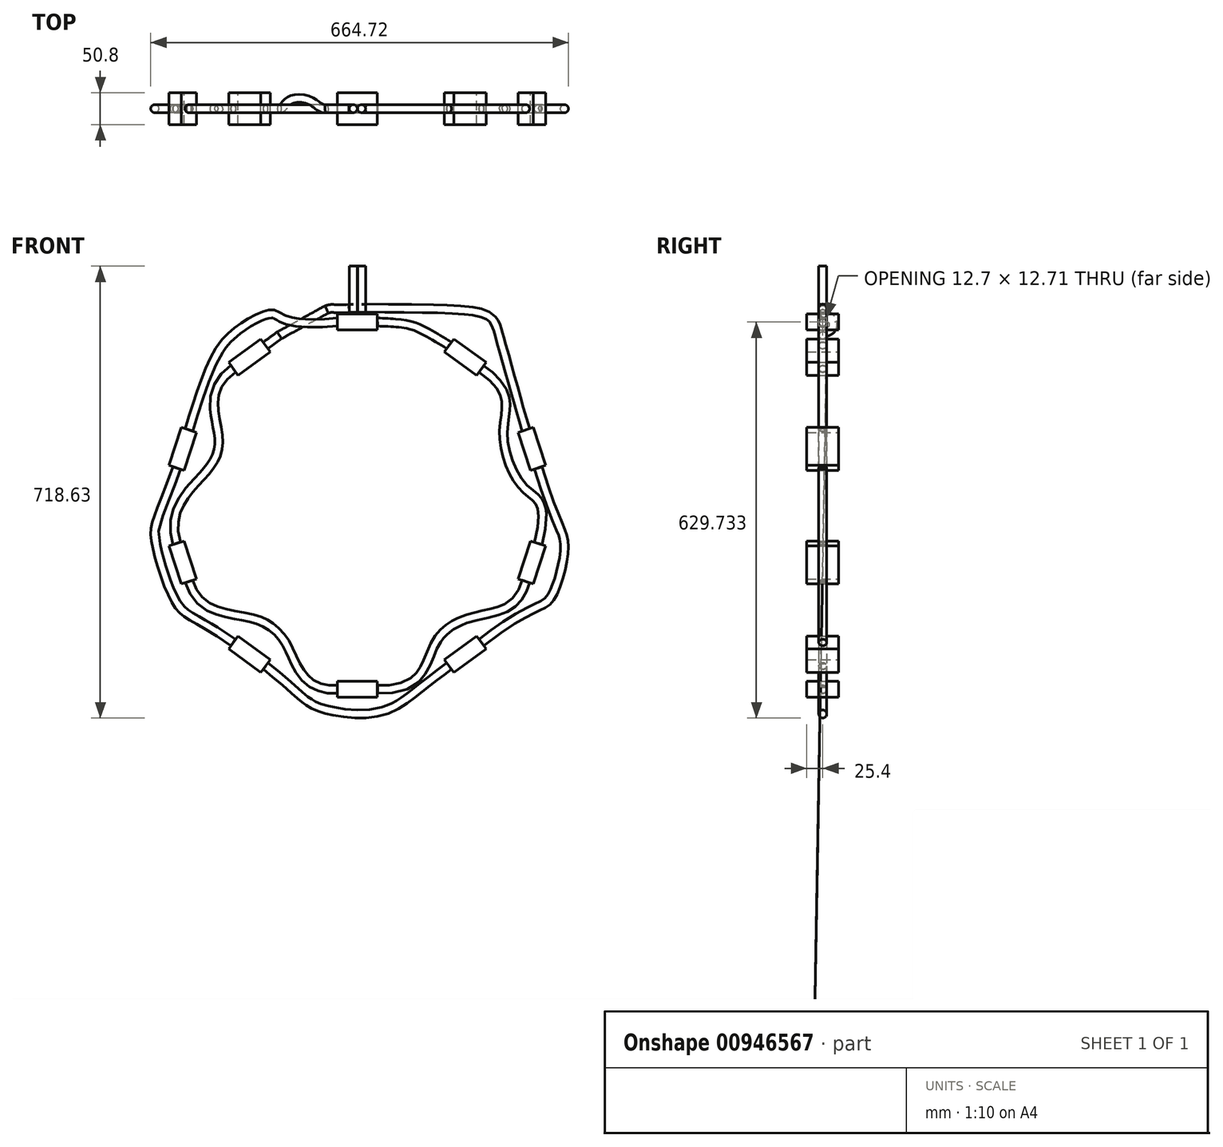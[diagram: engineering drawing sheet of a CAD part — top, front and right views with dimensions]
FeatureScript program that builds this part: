
annotation { "Feature Type Name" : "Feature", "Feature Type Description" : "" }
export const myFeature = defineFeature(function(context is Context, id is Id, definition is map)
    precondition{}
    {
        {
            var Q0;
            Q0=qCreatedBy(makeId("Front.planeOp"),FACE);
            var sketch = newSketch(context, id + "F0", { "sketchPlane" : qUnion([Q0])});
            skCircle(sketch, "E0", {"center": v(0, 0) * mm, "radius": 279.4 * mm});
            skCircle(sketch, "E1", {"center": v(0, 0) * mm, "radius": 304.8 * mm});
            skLineSegment(sketch, "E2", {"start": v(0, 279.4) * mm, "end": v(0, 304.8) * mm, "construction": true});
            skLineSegment(sketch, "E3.bottom", {"start": v(31.75, 304.8) * mm, "end": v(-31.75, 304.8) * mm});
            skLineSegment(sketch, "E3.top", {"start": v(31.75, 279.4) * mm, "end": v(-31.75, 279.4) * mm});
            skLineSegment(sketch, "E3.left", {"start": v(31.75, 304.8) * mm, "end": v(31.75, 279.4) * mm});
            skLineSegment(sketch, "E3.right", {"start": v(-31.75, 304.8) * mm, "end": v(-31.75, 279.4) * mm});
            skPoint(sketch, "E3.middle", {"position": v(0, 292.1) * mm});
            skSolve(sketch);
        }
        {
            var Q0;
            {var subQ0=sQuery(id+"F0.wireOp",EDGE,"E3.bottom");var subQ1=sQuery(id+"F0.wireOp",EDGE,"E1");var subQ2=makeQuery(id+"F0.imprint","INTERSECT",VERTEX,{"derivedFrom":[subQ1,subQ0]});Q0=makeQuery(id+"F0.imprint","IMPRINT",FACE,{"disambiguationData":[TD([[makeQuery(id+"F0.imprint","IMPRINT",EDGE,{"disambiguationData":[TD([[subQ2,1.0]])],"derivedFrom":subQ1}),-1.0]])]});}
            var Q1;
            {var subQ0=sQuery(id+"F0.wireOp",EDGE,"E3.bottom");var subQ1=sQuery(id+"F0.wireOp",EDGE,"E1");var subQ2=makeQuery(id+"F0.imprint","INTERSECT",VERTEX,{"derivedFrom":[subQ1,subQ0]});Q1=makeQuery(id+"F0.imprint","IMPRINT",FACE,{"disambiguationData":[TD([[makeQuery(id+"F0.imprint","IMPRINT",EDGE,{"disambiguationData":[TD([[subQ2,-1.0]])],"derivedFrom":subQ1}),-1.0]])]});}
            var Q2;
            {var subQ4=sQuery(id+"F0.wireOp",EDGE,"E1");var subQ5=makeQuery(id+"F0.imprint","INTERSECT",VERTEX,{"derivedFrom":[subQ4,sQuery(id+"F0.wireOp",EDGE,"E3.bottom")]});Q2=makeQuery(id+"F0.imprint","IMPRINT",FACE,{"disambiguationData":[TD([[makeQuery(id+"F0.imprint","IMPRINT",EDGE,{"disambiguationData":[TD([[subQ5,1.0]])],"derivedFrom":subQ4}),1.0]])]});}
            extrude(context, id + "F1", {"entities" : qUnion([Q0, Q1, Q2]), "endBound" : BoundingType.SYMMETRIC, "depth" : 50.8 * mm, "offsetDistance" : 25.4 * mm});
        }
        {
            var Q0;
            Q0=makeQuery(id+"F1.opExtrude","SWEPT_FACE",FACE,{"disambiguationData":[OSD([sQuery(id+"F0.wireOp",EDGE,"E3.left")])]});
            var sketch = newSketch(context, id + "F2", { "sketchPlane" : qUnion([Q0])});
            skCircle(sketch, "E4", {"center": v(0, 292.1) * mm, "radius": 4.76 * mm});
            skPoint(sketch, "E4.centerSnap0", {"position": v(-25.4, 292.1) * mm});
            skPoint(sketch, "E4.centerSnap1", {"position": v(0, 304.8) * mm});
            skCircle(sketch, "E5", {"center": v(0, 292.1) * mm, "radius": 6.35 * mm});
            skSolve(sketch);
        }
        {
            var Q0;
            Q0=qSketchRegion(id+"F2",true);
            var Q1;
            Q1=makeQuery(id+"F2.imprint","IMPRINT",FACE,{"disambiguationData":[TD([[makeQuery(id+"F2.imprint","IMPRINT",EDGE,{"derivedFrom":sQuery(id+"F2.wireOp",EDGE,"E4")}),1.0]])]});
            extrude(context, id + "F3", {"entities" : qUnion([Q0, Q1]), "operationType" : NewBodyOperationType.ADD, "depth" : 0.25 * mm, "offsetDistance" : 25.4 * mm});
        }
        {
            var Q0;
            Q0=makeQuery(id+"F1.opExtrude","SWEPT_FACE",FACE,{"disambiguationData":[OSD([sQuery(id+"F0.wireOp",EDGE,"E3.right")])]});
            var sketch = newSketch(context, id + "F4", { "sketchPlane" : qUnion([Q0])});
            skCircle(sketch, "E6", {"center": v(0, 292.1) * mm, "radius": 6.35 * mm});
            skSolve(sketch);
        }
        {
            var Q0;
            Q0=qSketchRegion(id+"F4",true);
            extrude(context, id + "F5", {"entities" : qUnion([Q0]), "operationType" : NewBodyOperationType.ADD, "depth" : 0.25 * mm, "offsetDistance" : 25.4 * mm});
        }
        {
            var Q0;
            Q0=makeQuery(id+"F1.opExtrude","SWEPT_BODY",BODY,{"disambiguationData":[OSD([sQuery(id+"F0.wireOp",EDGE,"E3.bottom"),sQuery(id+"F0.wireOp",EDGE,"E3.top"),sQuery(id+"F0.wireOp",EDGE,"E3.left"),sQuery(id+"F0.wireOp",EDGE,"E3.right")])]});
            var Q1;
            Q1=sQuery(id+"F0.wireOp",EDGE,"E0");
            circularPattern(context, id + "F6", {"operationType" : NewBodyOperationType.ADD, "entities" : qUnion([Q0]), "axis" : qUnion([Q1]), "angle" : 360 * degree, "instanceCount" : 10, "equalSpace" : true});
        }
        {
            var Q0;
            Q0=makeQuery(id+"F1.opExtrude","SWEPT_FACE",FACE,{"disambiguationData":[OSD([sQuery(id+"F0.wireOp",EDGE,"E3.bottom")])]});
            cPlane(context, id + "F7", {"entities" : qUnion([Q0]), "cplaneType" : CPlaneType.OFFSET, "offset" : 76.2 * mm, "width" : 152.4 * mm, "height" : 152.4 * mm});
        }
        {
            var Q0;
            Q0=qCreatedBy(id+"F7.planeOp",FACE);
            var sketch = newSketch(context, id + "F8", { "sketchPlane" : qUnion([Q0])});
            skCircle(sketch, "E7", {"center": v(6.6, 0) * mm, "radius": 6.35 * mm});
            skSolve(sketch);
        }
        {
            var Q0;
            Q0=makeQuery(id+"F8.imprint","IMPRINT",FACE,{"disambiguationData":[TD([[makeQuery(id+"F8.imprint","IMPRINT",EDGE,{"derivedFrom":sQuery(id+"F8.wireOp",EDGE,"tEIZt6W4-ahLr-2Sv8-WXze-j2Jn50dJCbSE")}),1.0]])]});
            var Q1;
            Q1=makeQuery(id+"F8.imprint","IMPRINT",FACE,{"disambiguationData":[TD([[makeQuery(id+"F8.imprint","IMPRINT",EDGE,{"derivedFrom":sQuery(id+"F8.wireOp",EDGE,"E7")}),1.0]])]});
            extrude(context, id + "F9", {"entities" : qUnion([Q0, Q1]), "oppositeDirection" : true, "depth" : 73.66 * mm, "offsetDistance" : 25.4 * mm});
        }
        {
            var Q0;
            Q0=makeQuery(id+"F9.opExtrude","CAP_FACE",FACE,{"disambiguationData":[OSD([sQuery(id+"F8.wireOp",EDGE,"E7")])],"isStart":false});
            var sketch = newSketch(context, id + "F10", { "sketchPlane" : qUnion([Q0])});
            skLineSegment(sketch, "E8", {"start": v(6.6, 0) * mm, "end": v(6.6, -6.35) * mm});
            skLineSegment(sketch, "E9", {"start": v(6.6, -6.35) * mm, "end": v(12.95, -6.35) * mm});
            skLineSegment(sketch, "E10", {"start": v(12.95, -6.35) * mm, "end": v(12.95, 6.35) * mm});
            skLineSegment(sketch, "E11", {"start": v(12.95, 6.35) * mm, "end": v(6.6, 6.35) * mm});
            skLineSegment(sketch, "E12", {"start": v(6.6, 6.35) * mm, "end": v(6.6, 0) * mm});
            skSolve(sketch);
        }
        {
            var Q0;
            Q0=qSketchRegion(id+"F10",true);
            extrude(context, id + "F11", {"entities" : qUnion([Q0]), "operationType" : NewBodyOperationType.ADD, "oppositeDirection" : true, "depth" : 12.7 * mm, "offsetDistance" : 25.4 * mm});
        }
        {
            var Q0;
            Q0=makeQuery(id+"F11.opExtrude","SWEPT_FACE",FACE,{"disambiguationData":[OSD([sQuery(id+"F10.wireOp",EDGE,"E10")])]});
            var sketch = newSketch(context, id + "F12", { "sketchPlane" : qUnion([Q0])});
            skCircle(sketch, "E13", {"center": v(0, 313.7) * mm, "radius": 4.76 * mm});
            skPoint(sketch, "E13.centerSnap0", {"position": v(6.35, 313.7) * mm});
            skSolve(sketch);
        }
        {
            var Q0;
            Q0=makeQuery(id+"F11.opExtrude","SWEPT_FACE",FACE,{"disambiguationData":[OSD([sQuery(id+"F10.wireOp",EDGE,"E10")])]});
            var sketch = newSketch(context, id + "F13", { "sketchPlane" : qUnion([Q0])});
            skCircle(sketch, "E14", {"center": v(0, 313.7) * mm, "radius": 6.35 * mm});
            skSolve(sketch);
        }
        {
            var Q0;
            Q0 = qSketchRegion(id + "F13", true);
            extrude(context, id + "F14", {"entities" : qUnion([Q0]), "operationType" : NewBodyOperationType.ADD, "depth" : 0.25 * mm, "offsetDistance" : 25.4 * mm});
        }
        {
            var Q0;
            Q0=makeQuery(id+"F9.opExtrude","SWEPT_BODY",BODY,{"disambiguationData":[OSD([sQuery(id+"F8.wireOp",EDGE,"E7")])]});
            var Q1;
            Q1=qCreatedBy(makeId("Right.planeOp"),FACE);
            mirror(context, id + "F15", {"entities" : qUnion([Q0]), "mirrorPlane" : qUnion([Q1])});
        }
        {
            var Q0;
            Q0=makeQuery(id+"F0.imprint","IMPRINT",FACE,{"disambiguationData":[TD([[makeQuery(id+"F0.imprint","IMPRINT",EDGE,{"derivedFrom":sQuery(id+"F0.wireOp",EDGE,"E0")}),1.0]])]});
            var sketch = newSketch(context, id + "F16", { "sketchPlane" : qUnion([Q0])});
            skFitSpline(sketch, "E15", {"points": [v(12.47, 313.93) * mm, v(226.12, 268.52) * mm, v(267.78, 120.27) * mm], "startDerivative": vector(1120.98, -8.53) * mm, "endDerivative": vector(74.4, -254) * mm});
            skFitSpline(sketch, "E16", {"points": [v(287.61, 60.07) * mm, v(329.49, -68.55) * mm, v(308.97, -144.06) * mm, v(197.38, -217.65) * mm], "startDerivative": vector(250.83, -825.95) * mm, "endDerivative": vector(-693.05, -541.05) * mm});
            skFitSpline(sketch, "E17", {"points": [v(146, -254.98) * mm, v(33.51, -328.63) * mm, v(-59.83, -321.14) * mm, v(-146, -254.98) * mm], "startDerivative": vector(-460.53, -336.9) * mm, "endDerivative": vector(-526.77, 425.26) * mm});
            skFitSpline(sketch, "E18", {"points": [v(-197.38, -217.65) * mm, v(-287.9, -153.94) * mm, v(-321.5, -54.37) * mm, v(-287.61, 60.07) * mm], "startDerivative": vector(-582.5, 403.5) * mm, "endDerivative": vector(248.06, 720.53) * mm});
            skFitSpline(sketch, "E19", {"points": [v(-268, 120.46) * mm, v(-189.22, 279.36) * mm, v(-136.83, 305.18) * mm, v(-31.75, 292.1) * mm], "startDerivative": vector(237.68, 786.19) * mm, "endDerivative": vector(869.95, 82.47) * mm});
            skFitSpline(sketch, "E20", {"points": [v(31.75, 292.1) * mm, v(146, 254.98) * mm], "startDerivative": vector(170.33, -6.81) * mm, "endDerivative": vector(172.43, -104.56) * mm});
            skFitSpline(sketch, "E21", {"points": [v(197.38, 217.65) * mm, v(232.4, 120.1) * mm, v(265.06, 28.4) * mm, v(287.61, -60.07) * mm], "startDerivative": vector(480.74, -335.97) * mm, "endDerivative": vector(-177.88, -652.27) * mm});
            skFitSpline(sketch, "E22", {"points": [v(268, -120.46) * mm, v(192.1, -175.03) * mm, v(124.52, -217.5) * mm, v(31.75, -292.1) * mm], "startDerivative": vector(-118.57, -426.02) * mm, "endDerivative": vector(-622.02, 31.85) * mm});
            skFitSpline(sketch, "E23", {"points": [v(-31.75, -292.1) * mm, v(-111.16, -223.64) * mm, v(-168.41, -178.83) * mm, v(-268, -120.46) * mm], "startDerivative": vector(-486.72, -26.66) * mm, "endDerivative": vector(-130.78, 434.77) * mm});
            skFitSpline(sketch, "E24", {"points": [v(-287.61, -60.07) * mm, v(-244.34, 50.19) * mm, v(-220.7, 108.69) * mm, v(-197.38, 217.65) * mm], "startDerivative": vector(-131.8, 444.42) * mm, "endDerivative": vector(405.83, 285.64) * mm});
            skSolve(sketch);
        }
        {
            var Q0;
            {var subQ1=makeQuery(id+"F0.imprint","IMPRINT",EDGE,{"derivedFrom":sQuery(id+"F0.wireOp",EDGE,"E0")});var subQ13=makeQuery(id+"F16.imprint","IMPRINT",VERTEX,{"derivedFrom":subQ1});Q0=makeQuery(id+"F16.imprint","IMPRINT",FACE,{"disambiguationData":[TD([[makeQuery(id+"F16.imprint","IMPRINT",EDGE,{"disambiguationData":[TD([[subQ13,1.0]])],"derivedFrom":subQ1}),1.0]])]});}
            var sketch = newSketch(context, id + "F17", { "sketchPlane" : qUnion([Q0])});
            skLineSegment(sketch, "E25", {"start": v(-146, 254.98) * mm, "end": v(-124.02, 270.95) * mm});
            skLineSegment(sketch, "E26", {"start": v(-49.14, 311.88) * mm, "end": v(-124.02, 270.95) * mm, "construction": true});
            skFitSpline(sketch, "E27", {"points": [v(-49.14, 311.88) * mm, v(-12.7, 313.7) * mm], "startDerivative": vector(36.27, 11.59) * mm, "endDerivative": vector(90.08, 5.48) * mm});
            skSolve(sketch);
        }
        {
            var Q0;
            Q0=sQuery(id+"F17.wireOp",EDGE,"E26");
            cPlane(context, id + "F18", {"entities" : qUnion([Q0]), "cplaneType" : CPlaneType.LINE_ANGLE, "offset" : 25.4 * mm, "angle" : 90 * degree, "width" : 152.4 * mm, "height" : 152.4 * mm});
        }
        {
            var Q0;
            Q0=qCreatedBy(id+"F18.planeOp",FACE);
            var sketch = newSketch(context, id + "F19", { "sketchPlane" : qUnion([Q0])});
            skFitSpline(sketch, "E28", {"points": [v(21.13, 0) * mm, v(36.36, 11.23) * mm, v(77.2, 12.63) * mm, v(106.46, 0) * mm], "startDerivative": vector(77.55, 0) * mm, "endDerivative": vector(90.06, 17.1) * mm});
            skSolve(sketch);
        }
        {
            var Q0;
            Q0=makeQuery(id+"F6.opPattern","COPY",FACE,{"derivedFrom":makeQuery(id+"F5.opExtrude","CAP_FACE",FACE,{"disambiguationData":[OSD([sQuery(id+"F4.wireOp",EDGE,"E6")])],"isStart":false}),"instanceName":"9"});
            var Q1;
            Q1=makeQuery(id+"F3.opExtrude","CAP_FACE",FACE,{"disambiguationData":[OSD([sQuery(id+"F2.wireOp",EDGE,"E5")])],"isStart":false});
            var Q2;
            Q2=sQuery(id+"F16.wireOp",EDGE,"E20");
            sweep(context, id + "F20", {"operationType" : NewBodyOperationType.ADD, "profiles" : qUnion([Q0, Q1]), "path" : qUnion([Q2])});
        }
        {
            var Q0;
            Q0=makeQuery(id+"F6.opPattern","COPY",FACE,{"derivedFrom":makeQuery(id+"F3.opExtrude","CAP_FACE",FACE,{"disambiguationData":[OSD([sQuery(id+"F2.wireOp",EDGE,"E5")])],"isStart":false}),"instanceName":"9"});
            var Q1;
            Q1=sQuery(id+"F16.wireOp",EDGE,"E21");
            sweep(context, id + "F21", {"operationType" : NewBodyOperationType.ADD, "profiles" : qUnion([Q0]), "path" : qUnion([Q1])});
        }
        {
            var Q0;
            Q0=makeQuery(id+"F6.opPattern","COPY",FACE,{"derivedFrom":makeQuery(id+"F3.opExtrude","CAP_FACE",FACE,{"disambiguationData":[OSD([sQuery(id+"F2.wireOp",EDGE,"E5")])],"isStart":false}),"instanceName":"7"});
            var Q1;
            Q1=sQuery(id+"F16.wireOp",EDGE,"E22");
            sweep(context, id + "F22", {"operationType" : NewBodyOperationType.ADD, "profiles" : qUnion([Q0]), "path" : qUnion([Q1])});
        }
        {
            var Q0;
            Q0=makeQuery(id+"F6.opPattern","COPY",FACE,{"derivedFrom":makeQuery(id+"F3.opExtrude","CAP_FACE",FACE,{"disambiguationData":[OSD([sQuery(id+"F2.wireOp",EDGE,"E5")])],"isStart":false}),"instanceName":"5"});
            var Q1;
            Q1=makeQuery(id+"F6.opPattern","COPY",EDGE,{"derivedFrom":makeQuery(id+"F3.opExtrude","CAP_EDGE",EDGE,{"disambiguationData":[OSD([sQuery(id+"F2.wireOp",EDGE,"E5")])],"isStart":false}),"instanceName":"5"});
            var Q2;
            Q2=sQuery(id+"F16.wireOp",EDGE,"E23");
            sweep(context, id + "F23", {"operationType" : NewBodyOperationType.ADD, "profiles" : qUnion([Q0]), "surfaceProfiles" : qUnion([Q1]), "path" : qUnion([Q2])});
        }
        {
            var Q0;
            Q0=makeQuery(id+"F6.opPattern","COPY",FACE,{"derivedFrom":makeQuery(id+"F3.opExtrude","CAP_FACE",FACE,{"disambiguationData":[OSD([sQuery(id+"F2.wireOp",EDGE,"E5")])],"isStart":false}),"instanceName":"3"});
            var Q1;
            Q1=sQuery(id+"F16.wireOp",EDGE,"E24");
            sweep(context, id + "F24", {"operationType" : NewBodyOperationType.ADD, "profiles" : qUnion([Q0]), "path" : qUnion([Q1])});
        }
        {
            var Q0;
            Q0=makeQuery(id+"F6.opPattern","COPY",FACE,{"derivedFrom":makeQuery(id+"F3.opExtrude","CAP_FACE",FACE,{"disambiguationData":[OSD([sQuery(id+"F2.wireOp",EDGE,"E5")])],"isStart":false}),"instanceName":"1"});
            var Q1;
            Q1=sQuery(id+"F19.wireOp",EDGE,"E28");
            var Q2;
            Q2=sQuery(id+"F17.wireOp",EDGE,"E25");
            var Q3;
            Q3=sQuery(id+"F17.wireOp",EDGE,"E27");
            sweep(context, id + "F25", {"operationType" : NewBodyOperationType.ADD, "profiles" : qUnion([Q0]), "path" : qUnion([Q1, Q2, Q3])});
        }
        {
            var Q0;
            Q0=makeQuery(id+"F5.opExtrude","CAP_FACE",FACE,{"disambiguationData":[OSD([sQuery(id+"F4.wireOp",EDGE,"E6")])],"isStart":false});
            var Q1;
            Q1=sQuery(id+"F16.wireOp",EDGE,"E19");
            sweep(context, id + "F26", {"operationType" : NewBodyOperationType.ADD, "profiles" : qUnion([Q0]), "path" : qUnion([Q1])});
        }
        {
            var Q0;
            Q0=makeQuery(id+"F6.opPattern","COPY",FACE,{"derivedFrom":makeQuery(id+"F5.opExtrude","CAP_FACE",FACE,{"disambiguationData":[OSD([sQuery(id+"F4.wireOp",EDGE,"E6")])],"isStart":false}),"instanceName":"2"});
            var Q1;
            Q1=sQuery(id+"F16.wireOp",EDGE,"E18");
            sweep(context, id + "F27", {"operationType" : NewBodyOperationType.ADD, "profiles" : qUnion([Q0]), "path" : qUnion([Q1])});
        }
        {
            var Q0;
            Q0=makeQuery(id+"F6.opPattern","COPY",FACE,{"derivedFrom":makeQuery(id+"F5.opExtrude","CAP_FACE",FACE,{"disambiguationData":[OSD([sQuery(id+"F4.wireOp",EDGE,"E6")])],"isStart":false}),"instanceName":"4"});
            var Q1;
            Q1=sQuery(id+"F16.wireOp",EDGE,"E17");
            sweep(context, id + "F28", {"operationType" : NewBodyOperationType.ADD, "profiles" : qUnion([Q0]), "path" : qUnion([Q1])});
        }
        {
            var Q0;
            Q0=makeQuery(id+"F6.opPattern","COPY",FACE,{"derivedFrom":makeQuery(id+"F5.opExtrude","CAP_FACE",FACE,{"disambiguationData":[OSD([sQuery(id+"F4.wireOp",EDGE,"E6")])],"isStart":false}),"instanceName":"6"});
            var Q1;
            Q1=sQuery(id+"F16.wireOp",EDGE,"E16");
            sweep(context, id + "F29", {"operationType" : NewBodyOperationType.ADD, "profiles" : qUnion([Q0]), "path" : qUnion([Q1])});
        }
        {
            var Q0;
            Q0=makeQuery(id+"F6.opPattern","COPY",FACE,{"derivedFrom":makeQuery(id+"F5.opExtrude","CAP_FACE",FACE,{"disambiguationData":[OSD([sQuery(id+"F4.wireOp",EDGE,"E6")])],"isStart":false}),"instanceName":"8"});
            var Q1;
            Q1=sQuery(id+"F16.wireOp",EDGE,"E15");
            sweep(context, id + "F30", {"operationType" : NewBodyOperationType.ADD, "profiles" : qUnion([Q0]), "path" : qUnion([Q1])});
        }
    });
